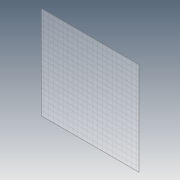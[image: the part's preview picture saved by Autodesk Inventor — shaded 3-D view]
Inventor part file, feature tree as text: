
AUTODESK INVENTOR PART (.ipt)
format: ipt  version: 2012 (Build 160160000, 160)  size: 81,408 bytes
history: native  units: in
note: dims shown in document units (in); Inventor stores cm internally (conversion verified against a paired STEP export)
features: extrude x1, sketch x1
ambient origin geometry x8: Origin, YZ Plane, XZ Plane, XY Plane, X Axis, Y Axis, Z Axis, Center Point
bodies: Solid1 (feature_tree)
feature tree (2):
  extrude  "Extrusion1"  Depth=45.75in
  sketch  "Sketch1"  dims[d0=48.0in d1=45.75in d2=0.125in d3=0.0in]
